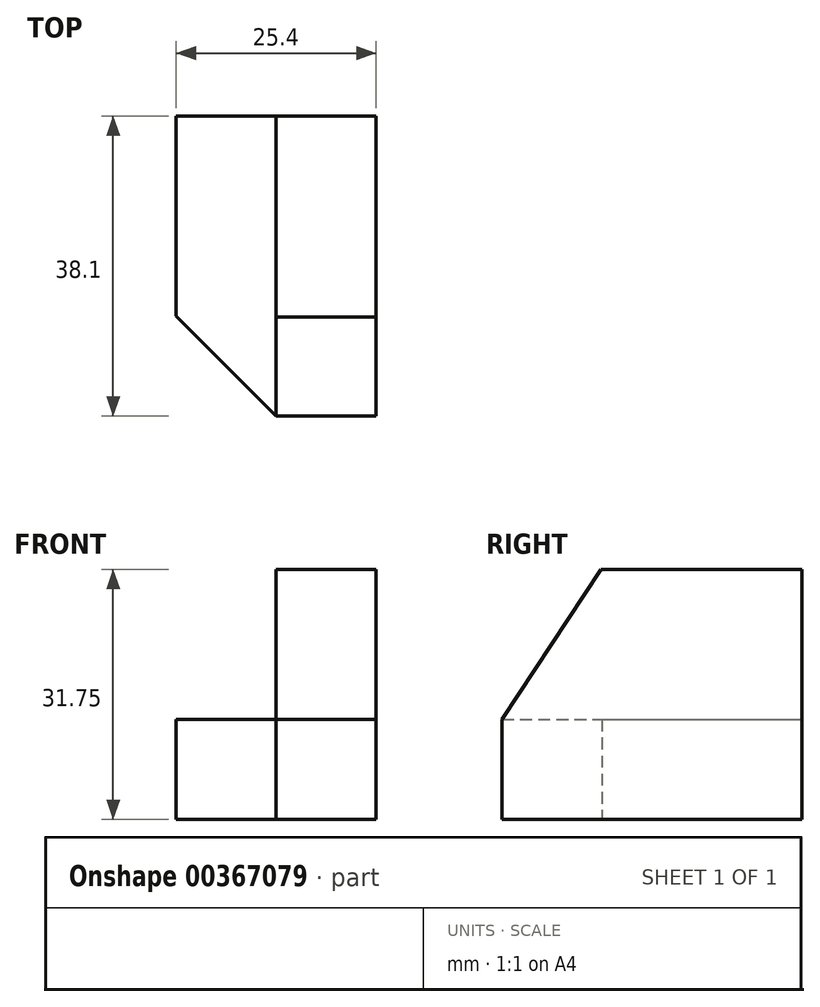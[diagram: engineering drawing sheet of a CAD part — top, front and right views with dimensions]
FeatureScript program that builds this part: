
annotation { "Feature Type Name" : "Feature", "Feature Type Description" : "" }
export const myFeature = defineFeature(function(context is Context, id is Id, definition is map)
    precondition{}
    {
        {
            var Q0;
            Q0=qCreatedBy(makeId("Front.planeOp"),FACE);
            var sketch = newSketch(context, id + "F0", { "sketchPlane" : qUnion([Q0])});
            skLineSegment(sketch, "E0", {"start": v(0, 0) * mm, "end": v(0, 31.75) * mm});
            skLineSegment(sketch, "E1", {"start": v(0, 31.75) * mm, "end": v(-12.7, 31.75) * mm});
            skLineSegment(sketch, "E2", {"start": v(-12.7, 31.75) * mm, "end": v(-12.7, 12.7) * mm});
            skLineSegment(sketch, "E3", {"start": v(-12.7, 12.7) * mm, "end": v(-25.4, 12.7) * mm});
            skLineSegment(sketch, "E4", {"start": v(-25.4, 12.7) * mm, "end": v(-25.4, 0) * mm});
            skLineSegment(sketch, "E5", {"start": v(-25.4, 0) * mm, "end": v(0, 0) * mm});
            skSolve(sketch);
        }
        {
            var Q0;
            Q0=makeQuery(id+"F0.imprint","IMPRINT",FACE,{"disambiguationData":[TD([[makeQuery(id+"F0.imprint","IMPRINT",EDGE,{"derivedFrom":sQuery(id+"F0.wireOp",EDGE,"E0")}),1.0]])]});
            extrude(context, id + "F1", {"entities" : qUnion([Q0]), "depth" : 38.1 * mm});
        }
        {
            var Q0;
            Q0=qCreatedBy(makeId("Right.planeOp"),FACE);
            var sketch = newSketch(context, id + "F2", { "sketchPlane" : qUnion([Q0])});
            skLineSegment(sketch, "E6", {"start": v(-38.1, 12.7) * mm, "end": v(-25.4, 31.94) * mm});
            skLineSegment(sketch, "E7", {"start": v(-25.4, 31.94) * mm, "end": v(-38.1, 31.94) * mm});
            skLineSegment(sketch, "E8", {"start": v(-38.1, 31.94) * mm, "end": v(-38.1, 12.7) * mm});
            skSolve(sketch);
        }
        {
            var Q0;
            Q0=makeQuery(id+"F2.imprint","IMPRINT",FACE,{"disambiguationData":[TD([[makeQuery(id+"F2.imprint","IMPRINT",EDGE,{"derivedFrom":sQuery(id+"F2.wireOp",EDGE,"E6")}),1.0]])]});
            extrude(context, id + "F3", {"entities" : qUnion([Q0]), "operationType" : NewBodyOperationType.REMOVE, "oppositeDirection" : true, "depth" : 25.4 * mm});
        }
        {
            var Q0;
            Q0=qCreatedBy(makeId("Top.planeOp"),FACE);
            var sketch = newSketch(context, id + "F4", { "sketchPlane" : qUnion([Q0])});
            skLineSegment(sketch, "E9", {"start": v(-12.7, -38.1) * mm, "end": v(-25.4, -25.4) * mm});
            skLineSegment(sketch, "E10", {"start": v(-25.4, -25.4) * mm, "end": v(-25.4, -38.1) * mm});
            skLineSegment(sketch, "E11", {"start": v(-25.4, -38.1) * mm, "end": v(-12.7, -38.1) * mm});
            skSolve(sketch);
        }
        {
            var Q0;
            Q0 = qSketchRegion(id + "F4", true);
            extrude(context, id + "F5", {"entities" : qUnion([Q0]), "operationType" : NewBodyOperationType.REMOVE, "depth" : 25.4 * mm});
        }
    });
